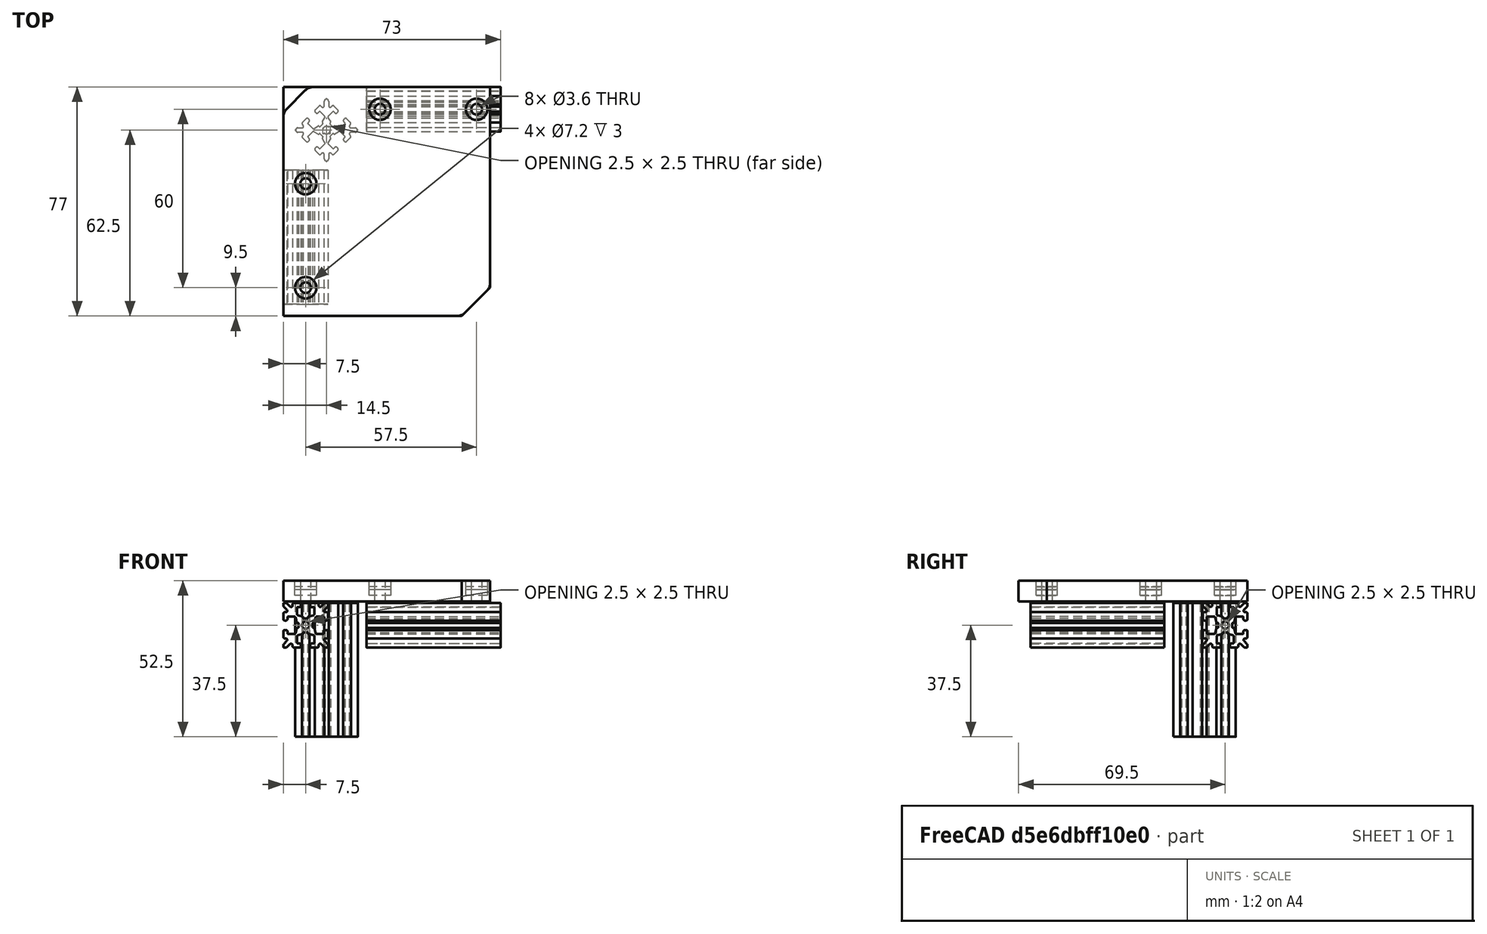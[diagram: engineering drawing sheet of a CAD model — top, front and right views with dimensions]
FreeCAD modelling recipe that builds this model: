
FCSTD DOCUMENT  (FreeCAD 0.15R4671 (Git))
Label: TopCornerCapMotor
License: All rights reserved
LicenseURL: http://en.wikipedia.org/wiki/All_rights_reserved
objects: Sketcher::SketchObject×3, Part::Feature×3, PartDesign::Pocket×2, PartDesign::Fillet×2, PartDesign::Pad×1, Mesh::Feature×1
note: 14 computed .brp shape members not serialized (recipe doc carries the construction recipe); baked Part::Feature solids carry a one-line shape summary decoded from their .brp

FEATURE [Sketcher::SketchObject] Sketch
  Placement = pos=(0,0,2) rot=(0,0,1;0rad)
  sketch-geometry (9):
    g0: LineSegment StartX=-7.5 StartY=7.5 StartZ=0 EndX=62.0538 EndY=7.5 EndZ=0
    g1: LineSegment StartX=62.0538 StartY=7.5 StartZ=0 EndX=62.0538 EndY=-59.9462 EndZ=0
    g2: LineSegment StartX=62.0538 StartY=-59.9462 StartZ=0 EndX=52.5 EndY=-69.5 EndZ=0
    g3: LineSegment StartX=52.5 StartY=-69.5 StartZ=0 EndX=-7.5 EndY=-69.5 EndZ=0
    g4: LineSegment StartX=-7.5 StartY=-69.5 StartZ=0 EndX=-7.5 EndY=7.5 EndZ=0
    g5: Circle CenterX=25 CenterY=0 CenterZ=0 NormalX=0 NormalY=0 NormalZ=1 Radius=1.8
    g6: Circle CenterX=57.5 CenterY=0 CenterZ=0 NormalX=0 NormalY=0 NormalZ=1 Radius=1.8
    g7: Circle CenterX=0 CenterY=-25 CenterZ=0 NormalX=0 NormalY=0 NormalZ=1 Radius=1.8
    g8: Circle CenterX=0 CenterY=-60 CenterZ=0 NormalX=0 NormalY=0 NormalZ=1 Radius=1.8
  constraints (16):
    c: Coincident(g0,g1)
    c: Coincident(g1,g2)
    c: Coincident(g2,g3)
    c: Coincident(g3,g4)
    c: Coincident(g4,g0)
    c: Horizontal(g3)
    c: Horizontal(g0)
    c: Vertical(g1)
    c: Vertical(g4)
    c: Angle(g2,g-2) = 0.785398
    c: DistanceX(g0) = -7.5
    c: DistanceY(g0) = 7.5
    c: Radius(g5) = 1.8
    c: Radius(g6) = 1.8
    c: Radius(g7) = 1.8
    c: Radius(g8) = 1.8
FEATURE [Part::Feature] Part__Feature  label="OB1515_45mm001"
  Placement = pos=(0,-20.5,-6) rot=(1,0,0;1.5708rad)
  shape: bbox 15 x 45 x 15 mm, 158 faces (baked)
FEATURE [Part::Feature] Part__Feature001  label="OB1515_45mm002"
  Placement = pos=(20.5,0,-6) rot=(0.57735,0.57735,0.57735;2.0944rad)
  shape: bbox 45 x 15 x 15 mm, 158 faces (baked)
FEATURE [Part::Feature] Part__Feature002  label="OB1515_45mm"
  Placement = pos=(7,-7,-43.5) rot=(0,0,1;0.785398rad)
  shape: bbox 21.01 x 21.01 x 45 mm, 158 faces (baked)
FEATURE [PartDesign::Pad] Pad
  Length = 7
  Length2 = 100
  Placement = pos=(0,0,2) rot=(0,0,1;0rad)
  Sketch = -> Sketch
  Type = 0
FEATURE [Sketcher::SketchObject] Sketch001
  Placement = pos=(0,0,9) rot=(0,0,1;0rad)
  Support = -> Pad [Face11]
  sketch-geometry (4):
    g0: Circle CenterX=57.5 CenterY=0 CenterZ=0 NormalX=0 NormalY=0 NormalZ=1 Radius=3.6
    g1: Circle CenterX=25 CenterY=0 CenterZ=0 NormalX=0 NormalY=0 NormalZ=1 Radius=3.6
    g2: Circle CenterX=0 CenterY=-25 CenterZ=0 NormalX=0 NormalY=0 NormalZ=1 Radius=3.6
    g3: Circle CenterX=0 CenterY=-60 CenterZ=0 NormalX=0 NormalY=0 NormalZ=1 Radius=3.6
  constraints (4):
    c: Radius(g0) = 3.6
    c: Radius(g1) = 3.6
    c: Radius(g2) = 3.6
    c: Radius(g3) = 3.6
FEATURE [PartDesign::Pocket] Pocket
  Length = 3
  Placement = pos=(0,0,2) rot=(0,0,1;0rad)
  Sketch = -> Sketch001
  Type = 0
FEATURE [Mesh::Feature] temp
FEATURE [Sketcher::SketchObject] Sketch002
  Placement = pos=(0,0,9) rot=(0,0,1;0rad)
  Support = -> Pocket [Face5]
  sketch-geometry (5):
    g0: LineSegment StartX=-8.5 StartY=-1 StartZ=0 EndX=-7.5 EndY=-1 EndZ=0
    g1: LineSegment StartX=-7.5 StartY=-1 StartZ=0 EndX=1 EndY=7.5 EndZ=0
    g2: LineSegment StartX=1 StartY=7.5 StartZ=0 EndX=1 EndY=8.5 EndZ=0
    g3: LineSegment StartX=1 StartY=8.5 StartZ=0 EndX=-8.5 EndY=8.5 EndZ=0
    g4: LineSegment StartX=-8.5 StartY=8.5 StartZ=0 EndX=-8.5 EndY=-1 EndZ=0
  constraints (5):
    c: Coincident(g0,g1)
    c: Coincident(g1,g2)
    c: Coincident(g2,g3)
    c: Coincident(g3,g4)
    c: Coincident(g4,g0)
FEATURE [PartDesign::Pocket] Pocket001
  Length = 5
  Placement = pos=(0,0,2) rot=(0,0,1;0rad)
  Sketch = -> Sketch002
  Type = 1
FEATURE [PartDesign::Fillet] Fillet
  Base = -> Pocket001 [Edge4,Edge24]
  Placement = pos=(0,0,2) rot=(0,0,1;0rad)
  Radius = 4
FEATURE [PartDesign::Fillet] Fillet001  label="TopCornerCapMotor"
  Base = -> Fillet [Edge30,Edge18]
  Placement = pos=(0,0,2) rot=(0,0,1;0rad)
  Radius = 4
